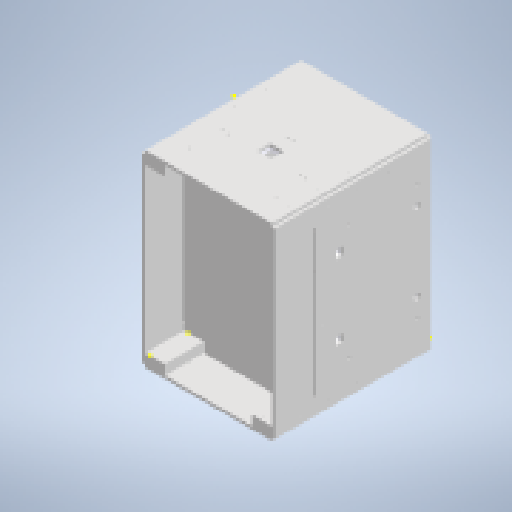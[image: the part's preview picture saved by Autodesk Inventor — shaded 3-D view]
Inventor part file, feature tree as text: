
AUTODESK INVENTOR PART (.ipt)
format: ipt  version: 2025.1 (Build 291241000, 241)  size: 1,120,768 bytes
history: native  units: mm
features: sketch x81, extrude x60, other x39, mirror x2, pattern_linear x1, imported_body x1
ambient origin geometry x8: Origin, YZ Plane, XZ Plane, XY Plane, X Axis, Y Axis, Z Axis, Center Point
bodies: Body1 (feature_tree), Body2 (feature_tree), Body3 (feature_tree), Body4 (feature_tree), Body5 (feature_tree), Body6 (feature_tree), Body7 (feature_tree), Body8 (feature_tree), Body9 (feature_tree), Body10 (feature_tree), Body11 (feature_tree), Body12 (feature_tree), Body13 (feature_tree), Body14 (feature_tree), Body15 (feature_tree), Body16 (feature_tree), Body17 (feature_tree), Body18 (feature_tree), Body19 (feature_tree), Body20 (feature_tree)
feature tree (184):
  other  "pilar 1"
  extrude  "Extrusão1"  Depth=100.0mm
  extrude  "Extrusão2"  Depth=935.0mm
  sketch  "Esboço3"  dims[d8=800.0mm d9=15.0mm d10=0.0mm]
  extrude  "Extrusão3"  Depth=15.0mm TaperAngle=0.0deg
  extrude  "Extrusão4"  Depth=50.0mm
  extrude  "Extrusão5"  Depth=650.0mm
  sketch  "Esboço8"  dims[d23=100.0mm d28=800.0mm d29=0.0mm]
  extrude  "Extrusão6"  Depth=15.0mm TaperAngle=0.0deg
  sketch  "Esboço10"  dims[d33=100.0mm d39=800.0mm d40=0.0mm]
  extrude  "Extrusão7"  Depth=800.0mm TaperAngle=0.0deg
  extrude  "Extrusão8"  Depth=15.0mm TaperAngle=0.0deg
  extrude  "Extrusão9"  Depth=800.0mm TaperAngle=0.0deg
  sketch  "Esboço14"  dims[d50=30.0mm d51=0.0mm d54=30.0mm d55=0.0mm]
  extrude  "Extrusão10"  Depth=15.0mm TaperAngle=0.0deg
  extrude  "Extrusão11"  Depth=30.0mm
  extrude  "Extrusão12"  Depth=600.0mm TaperAngle=0.0deg
  extrude  "Extrusão14"  Depth=30.0mm TaperAngle=0.0deg
  extrude  "Extrusão15"  Depth=500.0mm
  extrude  "Extrusão17"  Depth=30.0mm TaperAngle=0.0deg
  extrude  "Extrusão23"  Depth=875.0mm
  extrude  "Extrusão25"  Depth=45.0mm
  extrude  "Extrusão26"  Depth=30.0mm
  extrude  "Extrusão27"  Depth=30.0mm
  extrude  "Extrusão28"  Depth=400.0mm
  extrude  "Extrusão29"  Depth=3.5mm
  sketch  "Esboço39"  dims[d151=8000.0mm d152=0.0mm d163=3.5mm]
  extrude  "Extrusão30"  Depth=3.5mm
  sketch  "Esboço41"  dims[d167=3.5mm]
  sketch  "Esboço42"  dims[d169=3.5mm]
  extrude  "Extrusão32"  Depth=3.5mm
  extrude  "Extrusão33"  Depth=3.5mm
  extrude  "Extrusão34"  Depth=3.5mm
  extrude  "Extrusão35"  Depth=3.5mm
  pattern_linear  "Padrão retangular1"  Count1=800 Spacing1=0.0mm
  extrude  "Extrusão36"  Depth=3.5mm
  extrude  "Extrusão37"  Depth=3.5mm
  other  "Plano de trabalho1"
  mirror  "Espelhar2"
  mirror  "Espelhar3"
  sketch  "Esboço51"  dims[d208=3.5mm d209=0.0mm d216=20.0mm d217=0.0mm]
  sketch  "Esboço52"  dims[d218=15.0mm d219=0.0mm d220=15.0mm d221=0.0mm]
  sketch  "Esboço53"  dims[d222=15.0mm d223=7.5mm]
  sketch  "Esboço54"  dims[d224=935.0mm d225=467.5mm]
  extrude  "Extrusão39"  Depth=3.5mm TaperAngle=0.0deg
  sketch  "Esboço56"  dims[d231=40.0mm d232=958.0mm d233=0.0mm]
  extrude  "Extrusão40"  Depth=3.5mm
  extrude  "Extrusão41"  Depth=3.5mm
  extrude  "Extrusão42"  Depth=20.0mm TaperAngle=0.0deg
  sketch  "Esboço60"  dims[d242=100.0mm d243=15.0mm]
  extrude  "Extrusão43"  Depth=15.0mm TaperAngle=0.0deg
  sketch  "Esboço63"  dims[d249=20.0mm d250=6.0mm d251=0.0mm]
  sketch  "Esboço65"  dims[d252=95.0mm d253=15.0mm d254=0.0mm]
  extrude  "Extrusão45"  Depth=7.5mm
  sketch  "Esboço67"  dims[d259=10.0mm d260=5000.0mm d261=0.0mm]
  sketch  "Esboço68"  dims[d273=4.5mm d275=4.5mm]
  extrude  "Extrusão46"  Depth=467.5mm
  extrude  "Extrusão47"  Depth=50.0mm
  extrude  "Extrusão48"  Depth=40.0mm TaperAngle=0.0deg
  sketch  "Esboço73"  dims[d292=4.2mm d295=10.0mm d296=0.0mm]
  extrude  "Extrusão49"  Depth=45.0mm
  extrude  "Extrusão50"  Depth=200.0mm
  extrude  "Extrusão51"  Depth=30.0mm
  extrude  "Extrusão52"  Depth=15.0mm
  extrude  "Extrusão53"  Depth=20.0mm
  extrude  "Extrusão54"  Depth=6.0mm TaperAngle=0.0deg
  sketch  "Esboço80"  dims[d320=1910.5mm d321=0.0mm d322=70.0mm]
  extrude  "Extrusão55"  Depth=15.0mm TaperAngle=0.0deg
  extrude  "Extrusão56"  Depth=755.0mm
  extrude  "Extrusão57"  Depth=10.0mm TaperAngle=0.0deg
  extrude  "Extrusão58"  Depth=4.5mm
  extrude  "Extrusão59"  Depth=10.0mm TaperAngle=0.0deg
  extrude  "Extrusão60"  Depth=4.2mm
  extrude  "Extrusão61"  Depth=10.0mm TaperAngle=0.0deg
  sketch  "Esboço88"  dims[d354=62.0mm]
  extrude  "Extrusão62"  Depth=16.82mm
  extrude  "Extrusão63"  Depth=45.0mm TaperAngle=0.0deg
  extrude  "Extrusão64"  Depth=8.0mm
  sketch  "Esboço92"  dims[d364=3.5mm]
  extrude  "Extrusão66"  Depth=965.0mm TaperAngle=0.0deg
  extrude  "Extrusão67"  Depth=95.0mm
  extrude  "Extrusão68"  Depth=12.5mm
  sketch  "Esboço97"  dims[d370=75.0mm]
  extrude  "Extrusão69"  Depth=70.0mm
  extrude  "Extrusão70"  Depth=100.0mm
  extrude  "Extrusão71"  Depth=15.0mm
  extrude  "Extrusão72"  Depth=15.0mm
  sketch  "Esboço1"  dims[d1=50.0mm d2=100.0mm]
  sketch  "Esboço2"  dims[d4=800.0mm d5=0.0mm d7=935.0mm]
  other  "parede grande 1"
  sketch  "Esboço4"  dims[d11=100.0mm d12=50.0mm]
  other  "pilar 2"
  sketch  "Esboço6"  dims[d15=800.0mm d16=0.0mm d19=650.0mm]
  other  "parede pequena 1"
  sketch  "Esboço7"  dims[d20=800.0mm d21=15.0mm d22=0.0mm]
  other  "pilar 3"
  sketch  "Esboço9"  dims[d30=935.0mm d31=15.0mm d32=0.0mm]
  other  "parede grande 2"
  sketch  "Esboço11"  dims[d41=15.0mm d42=0.0mm d43=15.0mm d44=0.0mm]
  other  "pilar 4"
  sketch  "Esboço12"  dims[d45=600.0mm d46=30.0mm]
  other  "parede pequena 2"
  sketch  "Esboço13"  dims[d47=600.0mm d48=785.0mm d49=0.0mm]
  imported_body  "base"
  sketch  "Esboço15"  dims[d58=600.0mm d59=500.0mm]
  other  "isopor grande 1"
  sketch  "Esboço16"  dims[d60=600.0mm d61=30.0mm d62=0.0mm]
  other  "isoport grande 2"
  sketch  "Esboço17"  dims[d63=45.0mm d64=875.0mm]
  other  "isoport pequeno 1"
  sketch  "Esboço19"  dims[d65=15.0mm d66=0.0mm d71=45.0mm]
  other  "Contorno projetado4"
  other  "isopor pequeno 2"
  sketch  "Esboço20"  dims[d72=15.0mm d73=0.0mm d98=30.0mm]
  other  "moldura"
  sketch  "Esboço22"  dims[d99=585.0mm d100=0.0mm d104=30.0mm]
  sketch  "Esboço29"  dims[d105=585.0mm d106=0.0mm d111=400.0mm]
  other  "isopor interna 1"
  sketch  "Esboço31"  dims[d112=75.0mm d115=3.5mm]
  other  "isopor interno 2"
  sketch  "Esboço35"  dims[d119=3.5mm d123=3.5mm]
  sketch  "Esboço36"  dims[d127=3.5mm d131=3.5mm]
  sketch  "Esboço37"  dims[d132=8000.0mm d133=0.0mm d145=3.5mm]
  sketch  "Esboço38"  dims[d146=3.5mm d148=3.5mm]
  sketch  "Esboço40"  dims[d165=3.5mm]
  sketch  "Esboço45"  dims[d171=3.5mm d172=8000.0mm d173=0.0mm]
  other  "Contorno projetado8"
  other  "Contorno projetado9"
  other  "Contorno projetado10"
  other  "Contorno projetado11"
  sketch  "Esboço46"  dims[d184=3.5mm d186=3.5mm]
  other  "Contorno projetado12"
  sketch  "Esboço47"  dims[d188=3.5mm d190=3.5mm]
  other  "Contorno projetado13"
  sketch  "Esboço48"  dims[d192=3.5mm d193=8000.0mm d194=0.0mm]
  other  "Contorno projetado14"
  sketch  "Esboço49"  dims[d198=3.5mm d201=3.5mm]
  other  "Referência1"
  other  "Referência2"
  other  "Referência3"
  other  "Referência4"
  other  "Referência5"
  sketch  "Esboço50"  dims[d204=3.5mm d207=3.5mm]
  sketch  "Esboço55"  dims[d226=958.0mm d227=0.0mm d228=50.0mm d230=175.0mm]
  sketch  "Esboço57"  dims[d234=45.0mm d235=45.0mm]
  other  "vidro"
  sketch  "Esboço58"  dims[d236=5000.0mm d237=0.0mm d239=200.0mm]
  sketch  "Esboço59"  dims[d240=70.0mm d241=30.0mm]
  sketch  "Esboço61"  dims[d246=30.0mm d247=0.0mm d248=20.0mm]
  sketch  "Esboço66"  dims[d255=15.0mm d256=0.0mm d258=755.0mm]
  sketch  "Esboço69"  dims[d276=5000.0mm d277=0.0mm d280=10.0mm d281=0.0mm]
  sketch  "Esboço72"  dims[d285=4.2mm d286=4.2mm]
  sketch  "Esboço74"  dims[d297=16.82mm d298=16.82mm]
  sketch  "Esboço75"  dims[d300=15.0mm d301=45.0mm d302=0.0mm]
  sketch  "Esboço76"  dims[d304=8.0mm d306=8.0mm]
  sketch  "Esboço77"  dims[d307=40000.0mm d308=0.0mm d313=965.0mm d314=0.0mm]
  sketch  "Esboço78"  dims[d316=75.0mm d317=95.0mm]
  other  "Sólido21"
  sketch  "Esboço79"  dims[d318=85.0mm d319=12.5mm]
  sketch  "Esboço81"  dims[d323=100.0mm d324=167.5mm]
  other  "interno mdf"
  sketch  "Esboço82"  dims[d325=350.0mm d328=15.0mm]
  other  "Sólido24"
  sketch  "Esboço83"  dims[d330=30.0mm d332=15.0mm]
  other  "Sólido25"
  sketch  "Esboço84"  dims[d333=45.0mm d334=0.0mm]
  sketch  "Esboço85"  dims[d350=45000.0mm d351=0.0mm]
  sketch  "Esboço86"  dims[d352=20.0mm]
  sketch  "Esboço87"  dims[d353=20.0mm]
  sketch  "Esboço89"  dims[d355=62.0mm]
  sketch  "Esboço90"  dims[d358=3.5mm]
  sketch  "Esboço91"  dims[d361=3.5mm]
  sketch  "Esboço94"  dims[d367=3.5mm]
  sketch  "Esboço95"  dims[d368=4.0mm]
  sketch  "Esboço96"  dims[d369=75.0mm]
  other  "Sólido26"
  sketch  "Esboço98"  dims[d371=75.0mm]
  sketch  "Esboço99"  dims[d372=2000.0mm d373=0.0mm]
  other  "Sólido27"
  sketch  "Esboço100"  dims[d374=50.0mm]
  sketch  "Esboço101"  dims[d376=75.0mm d377=20.0mm d378=409.03mm d379=16.0mm d380=650.0mm d381=0.0mm d382=30.0mm d383=0.0mm d384=30.0mm d385=0.0mm d386=50000.0mm d387=0.0mm d388=4.513mm d389=4.513mm d390=11.51mm d391=5000.0mm d392=5.0mm d393=0.0mm d394=0.0mm d395=4.513mm d396=4.513mm d397=11.51mm d398=33.595mm d399=33.595mm d400=239.566mm d401=5000.0mm d402=5.0mm d403=0.0mm d404=0.0mm d405=239.566mm d406=11.51mm d407=34.468mm d408=15.0mm d409=7.5mm d410=17.234mm d411=5000.0mm d412=0.0mm d413=34.468mm d414=15.0mm d415=42.5mm d416=13.842mm d417=5000.0mm d418=0.0mm d419=4.531mm d420=4.531mm d421=11.51mm d422=5.724mm d423=5000.0mm d424=0.0mm d431=40.0mm d432=2.398mm d433=40.0mm d434=2.398mm d435=40.0mm d436=5000.0mm d437=0.0mm d438=40.0mm d439=40.0mm d440=40.0mm d442=2.398mm d443=5000.0mm d444=0.0mm d452=1000.0mm d453=0.0mm d454=75.0mm d455=75.0mm d456=75.0mm d457=10.0mm d458=10.0mm d459=10.0mm d460=10.0mm d461=30.0mm d462=2000.0mm d463=0.0mm d464=10.0mm d465=10.0mm d466=10.0mm d467=30.0mm d468=10.0mm d469=10.0mm d470=2000.0mm d471=0.0mm d472=105.0mm d473=105.0mm d474=15.0mm d475=0.0mm d478=695.0mm d480=15.0mm d481=0.0mm d483=175.0mm d484=175.0mm d485=20.0mm d486=175.0mm d487=175.0mm d489=6.0mm d490=0.0mm d491=20.0mm d492=25.0mm d494=4.2mm d495=4.2mm d497=30.0mm d498=5000.0mm d499=0.0mm d503=4.2mm d504=4.2mm d506=12000.0mm d507=0.0mm d17=0.5mm d18=0.872665mm d79=0.5mm d80=0.872665mm d81=0.5mm d82=0.872665mm d262=0.5mm d263=0.872665mm d450=0.5mm d451=0.872665mm]
  other  "<userpath>\Documents\1-CoisasSerias\UTFPR\2024-2\Oficina\Estrutura\Montagem1 - Copia.iam"
  other  "Montagem1 - Copia.iam"
  other  "cooler 40x40:1"
